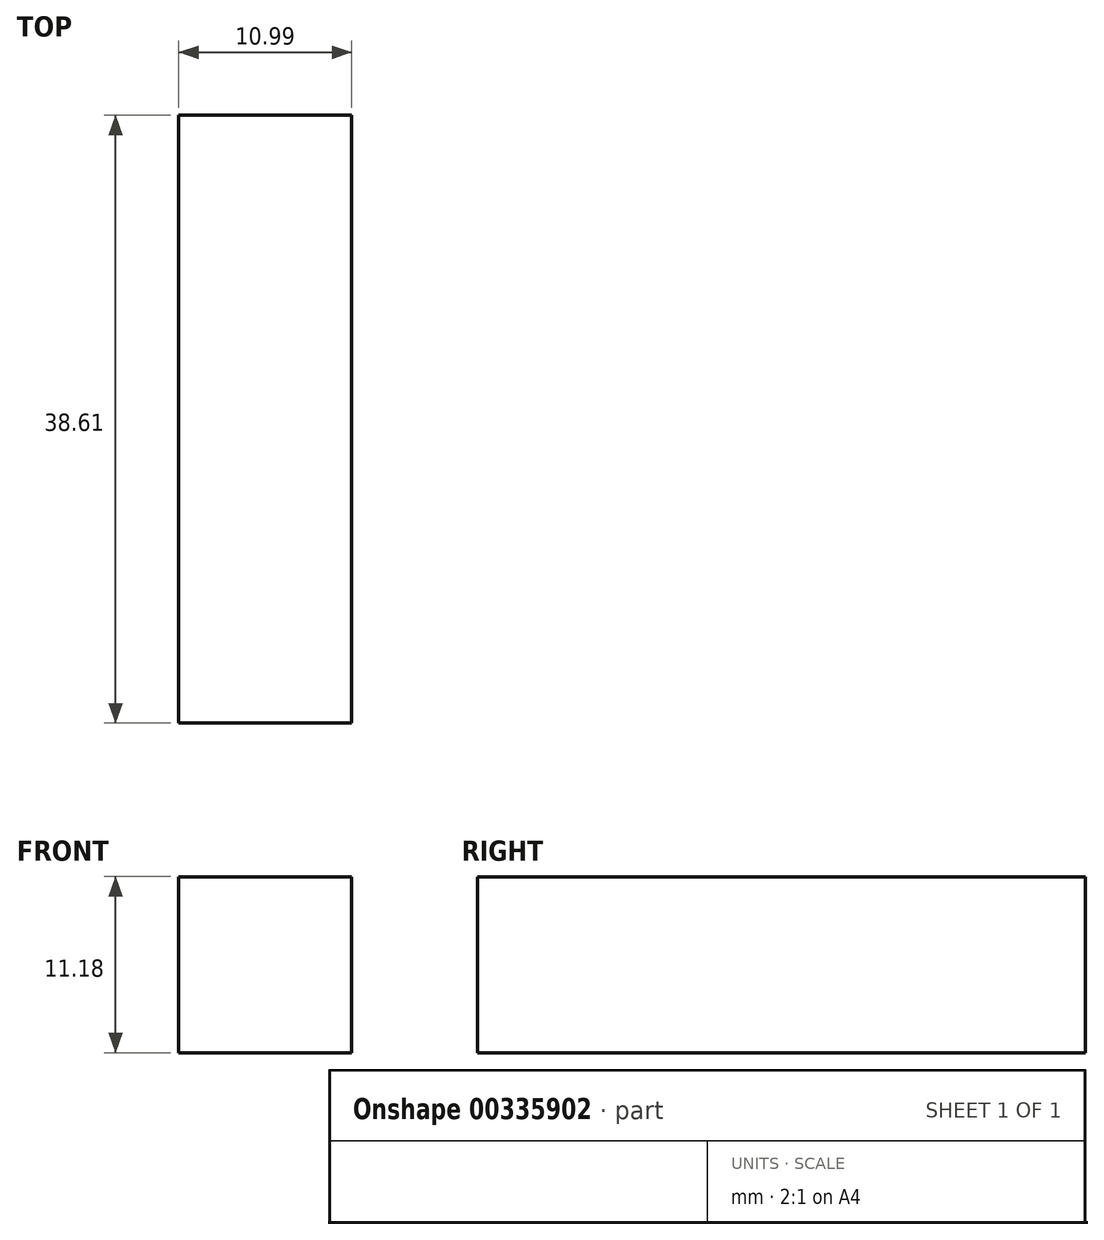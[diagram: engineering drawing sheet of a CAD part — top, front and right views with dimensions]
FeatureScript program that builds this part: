
annotation { "Feature Type Name" : "Feature", "Feature Type Description" : "" }
export const myFeature = defineFeature(function(context is Context, id is Id, definition is map)
    precondition{}
    {
        {
            var Q0;
            Q0=qCreatedBy(makeId("Front.planeOp"),FACE);
            var sketch = newSketch(context, id + "F0", { "sketchPlane" : qUnion([Q0])});
            skLineSegment(sketch, "E0.bottom", {"start": v(0, 0) * mm, "end": v(-10.99, 0) * mm});
            skLineSegment(sketch, "E0.top", {"start": v(0, 11.18) * mm, "end": v(-10.99, 11.18) * mm});
            skLineSegment(sketch, "E0.left", {"start": v(0, 0) * mm, "end": v(0, 11.18) * mm});
            skLineSegment(sketch, "E0.right", {"start": v(-10.99, 0) * mm, "end": v(-10.99, 11.18) * mm});
            skSolve(sketch);
        }
        {
            var Q0;
            Q0=makeQuery(id+"F0.imprint","IMPRINT",FACE,{"disambiguationData":[TD([[makeQuery(id+"F0.imprint","IMPRINT",EDGE,{"derivedFrom":sQuery(id+"F0.wireOp",EDGE,"E0.bottom")}),-1.0]])]});
            extrude(context, id + "F1", {"entities" : qUnion([Q0]), "depth" : 38.6 * mm});
        }
    });
